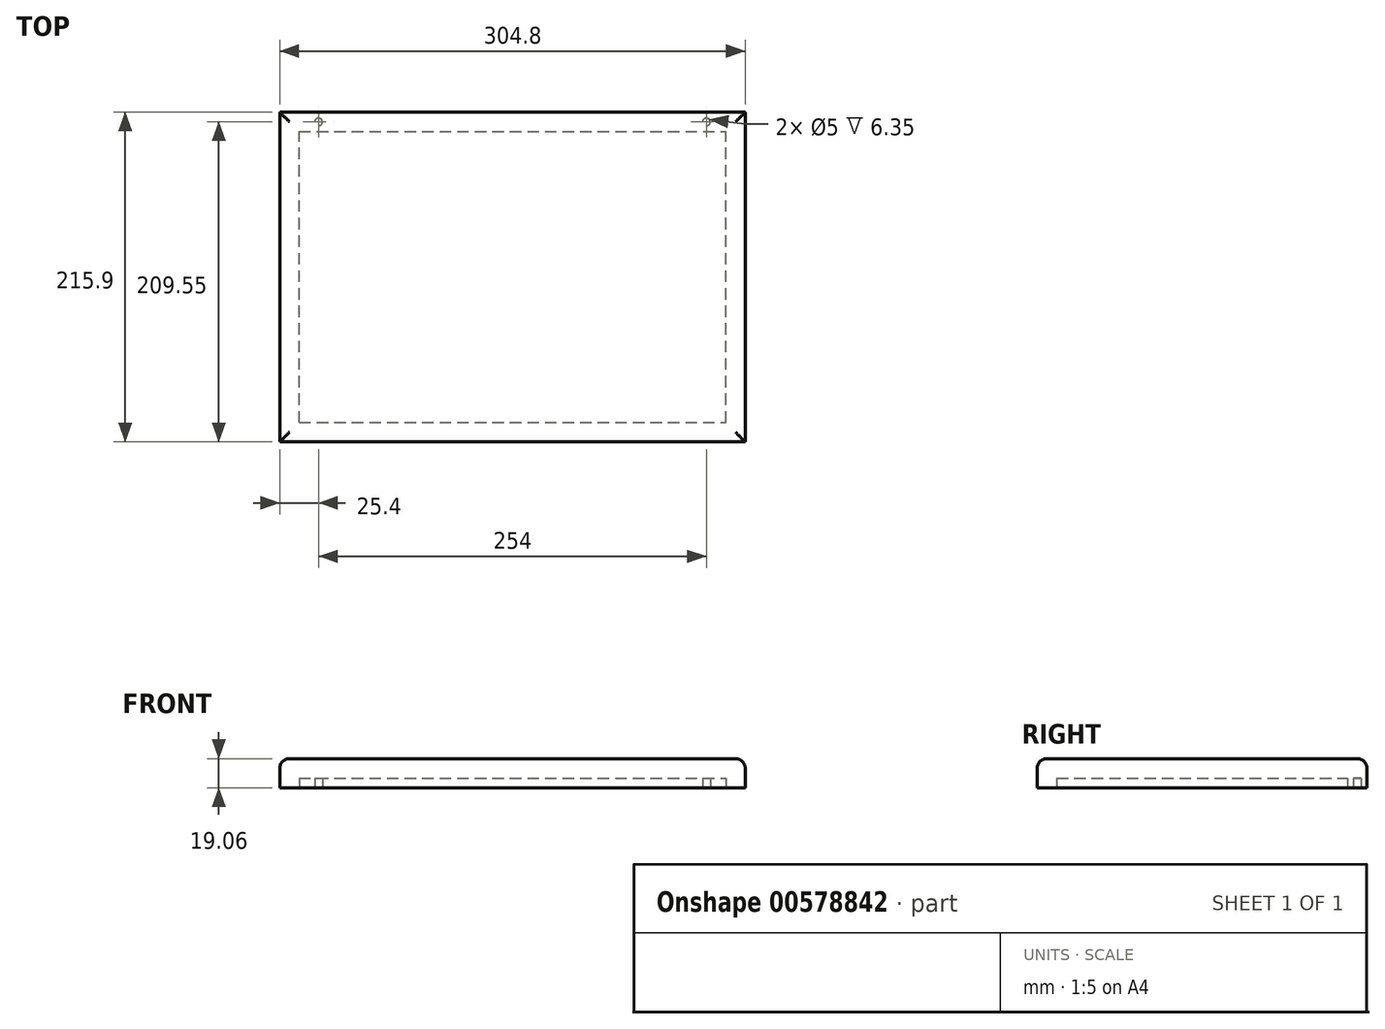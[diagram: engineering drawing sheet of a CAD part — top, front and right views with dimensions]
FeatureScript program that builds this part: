
annotation { "Feature Type Name" : "Feature", "Feature Type Description" : "" }
export const myFeature = defineFeature(function(context is Context, id is Id, definition is map)
    precondition{}
    {
        {
            var Q0;
            Q0=qCreatedBy(makeId("Front.planeOp"),FACE);
            var sketch = newSketch(context, id + "F0", { "sketchPlane" : qUnion([Q0])});
            skLineSegment(sketch, "E0.bottom", {"start": v(152.4, 9.53) * mm, "end": v(-152.4, 9.53) * mm});
            skLineSegment(sketch, "E0.top", {"start": v(152.4, -9.53) * mm, "end": v(-152.4, -9.53) * mm});
            skLineSegment(sketch, "E0.left", {"start": v(152.4, 9.53) * mm, "end": v(152.4, -9.53) * mm});
            skLineSegment(sketch, "E0.right", {"start": v(-152.4, 9.53) * mm, "end": v(-152.4, -9.53) * mm});
            skPoint(sketch, "E0.middle", {"position": v(0, 0) * mm});
            skSolve(sketch);
        }
        {
            var Q0;
            Q0=makeQuery(id+"F0.imprint","IMPRINT",FACE,{"disambiguationData":[TD([[makeQuery(id+"F0.imprint","IMPRINT",EDGE,{"derivedFrom":sQuery(id+"F0.wireOp",EDGE,"E0.bottom")}),1.0]])]});
            extrude(context, id + "F1", {"entities" : qUnion([Q0]), "depth" : 215.9 * mm, "offsetDistance" : 25.4 * mm});
        }
        {
            var Q0;
            Q0=makeQuery(id+"F1.opExtrude","SWEPT_FACE",FACE,{"disambiguationData":[OSD([sQuery(id+"F0.wireOp",EDGE,"E0.top")])]});
            var sketch = newSketch(context, id + "F2", { "sketchPlane" : qUnion([Q0])});
            skLineSegment(sketch, "E1.bottom", {"start": v(-139.7, 203.2) * mm, "end": v(139.7, 203.2) * mm});
            skLineSegment(sketch, "E1.top", {"start": v(-139.7, 12.7) * mm, "end": v(139.7, 12.7) * mm});
            skLineSegment(sketch, "E1.left", {"start": v(-139.7, 203.2) * mm, "end": v(-139.7, 12.7) * mm});
            skLineSegment(sketch, "E1.right", {"start": v(139.7, 203.2) * mm, "end": v(139.7, 12.7) * mm});
            skSolve(sketch);
        }
        {
            var Q0;
            Q0=makeQuery(id+"F2.imprint","IMPRINT",FACE,{"disambiguationData":[TD([[makeQuery(id+"F2.imprint","IMPRINT",EDGE,{"derivedFrom":sQuery(id+"F2.wireOp",EDGE,"E1.bottom")}),-1.0]])]});
            extrude(context, id + "F3", {"entities" : qUnion([Q0]), "operationType" : NewBodyOperationType.REMOVE, "oppositeDirection" : true, "depth" : 6.35 * mm, "offsetDistance" : 25.4 * mm});
        }
        {
            var Q0;
            Q0=makeQuery(id+"F1.opExtrude","SWEPT_EDGE",EDGE,{"disambiguationData":[OSD([sQuery(id+"F0.wireOp",EDGE,"E0.bottom"),sQuery(id+"F0.wireOp",EDGE,"E0.right")])]});
            var Q1;
            Q1=makeQuery(id+"F1.opExtrude","CAP_EDGE",EDGE,{"disambiguationData":[OSD([sQuery(id+"F0.wireOp",EDGE,"E0.bottom")])],"isStart":false});
            var Q2;
            Q2=makeQuery(id+"F1.opExtrude","SWEPT_EDGE",EDGE,{"disambiguationData":[OSD([sQuery(id+"F0.wireOp",EDGE,"E0.bottom"),sQuery(id+"F0.wireOp",EDGE,"E0.left")])]});
            var Q3;
            Q3=makeQuery(id+"F1.opExtrude","CAP_EDGE",EDGE,{"disambiguationData":[OSD([sQuery(id+"F0.wireOp",EDGE,"E0.bottom")])],"isStart":true});
            fillet(context, id + "F4", {"entities" : qUnion([Q0, Q1, Q2, Q3]), "radius" : 6.35 * mm, "tangentPropagation" : true, "allowEdgeOverflow" : false});
        }
        {
            var Q0;
            Q0=makeQuery(id+"F1.opExtrude","SWEPT_FACE",FACE,{"disambiguationData":[OSD([sQuery(id+"F0.wireOp",EDGE,"E0.top")])]});
            var sketch = newSketch(context, id + "F5", { "sketchPlane" : qUnion([Q0])});
            skCircle(sketch, "E2", {"center": v(-127, 6.35) * mm, "radius": 2.5 * mm});
            skCircle(sketch, "E3", {"center": v(127, 6.35) * mm, "radius": 2.5 * mm});
            skSolve(sketch);
        }
        {
            var Q0;
            Q0=makeQuery(id+"F5.imprint","IMPRINT",FACE,{"disambiguationData":[TD([[makeQuery(id+"F5.imprint","IMPRINT",EDGE,{"derivedFrom":sQuery(id+"F5.wireOp",EDGE,"E3")}),1.0]])]});
            var Q1;
            Q1=makeQuery(id+"F5.imprint","IMPRINT",FACE,{"disambiguationData":[TD([[makeQuery(id+"F5.imprint","IMPRINT",EDGE,{"derivedFrom":sQuery(id+"F5.wireOp",EDGE,"E2")}),1.0]])]});
            extrude(context, id + "F6", {"entities" : qUnion([Q0, Q1]), "operationType" : NewBodyOperationType.REMOVE, "oppositeDirection" : true, "depth" : 6.35 * mm, "offsetDistance" : 25.4 * mm});
        }
    });
